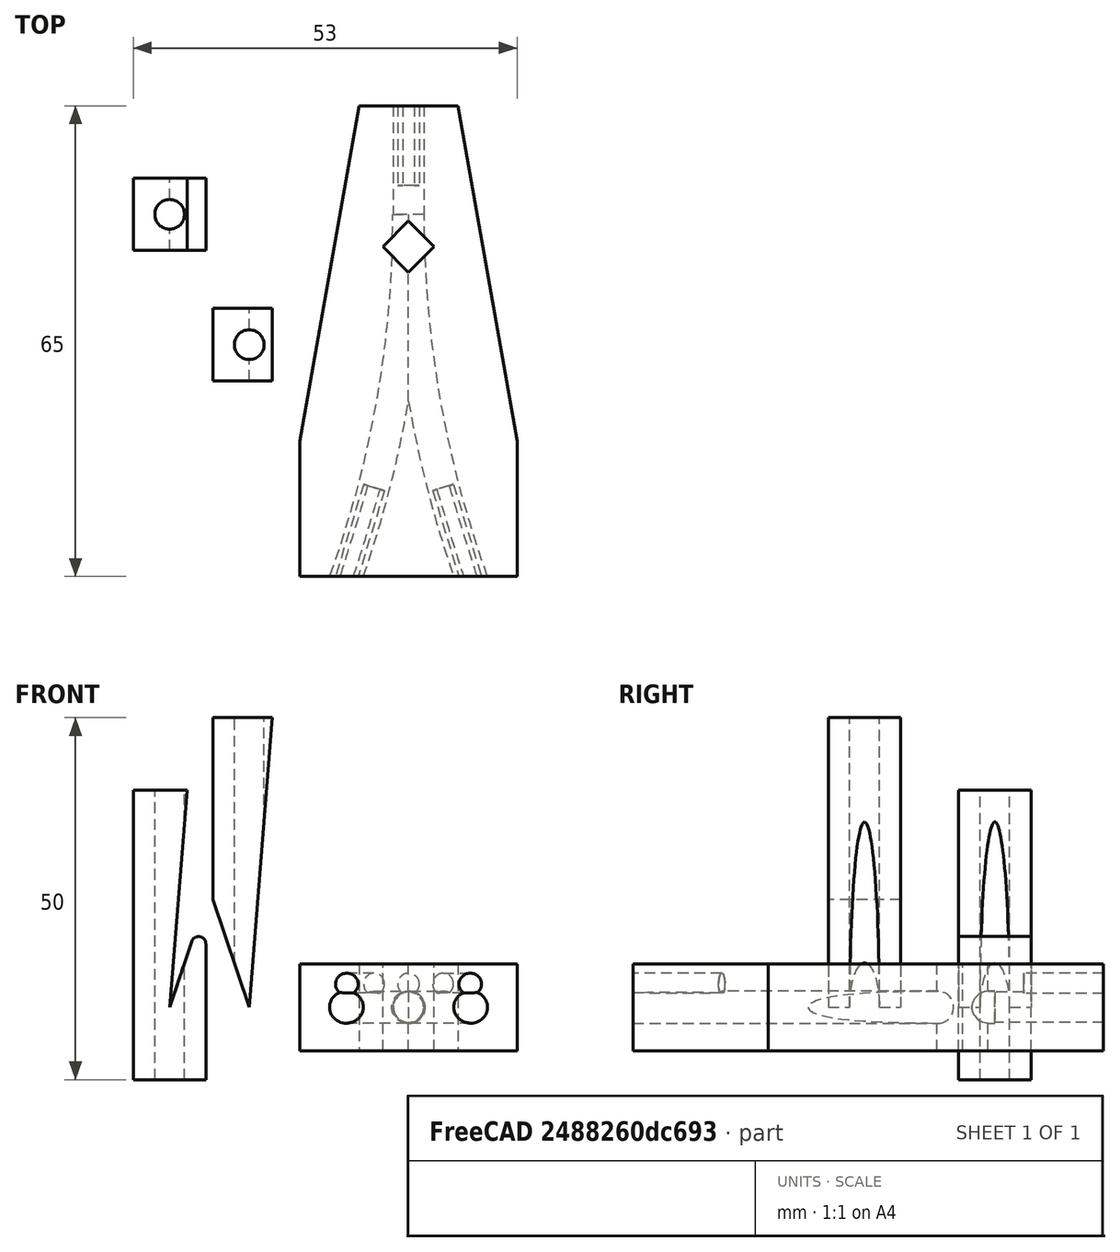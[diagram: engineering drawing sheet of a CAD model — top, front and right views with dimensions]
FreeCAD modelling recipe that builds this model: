
FCSTD DOCUMENT  (FreeCAD 0.15R4671 (Git))
Label: ptfe-traintracks
License: All rights reserved
LicenseURL: http://en.wikipedia.org/wiki/All_rights_reserved
objects: Part::Cut×17, Part::Box×12, Part::Cylinder×6, Part::Torus×2, Part::Fillet×1, Part::Mirroring×1
note: 39 computed .brp shape members not serialized (recipe doc carries the construction recipe); baked Part::Feature solids carry a one-line shape summary decoded from their .brp

FEATURE [Part::Torus] Torus
  Angle1 = -180
  Angle2 = 180
  Angle3 = 360
  Placement = pos=(-150,0,0) rot=(0,0,1;0rad)
  Radius1 = 150
  Radius2 = 2.2
FEATURE [Part::Torus] Torus001
  Angle1 = -180
  Angle2 = 180
  Angle3 = 360
  Placement = pos=(150,0,0) rot=(0,0,1;0rad)
  Radius1 = 150
  Radius2 = 2.2
FEATURE [Part::Box] Box  label="Cube"
  Height = 10
  Length = 700
  Placement = pos=(-350,0,-4) rot=(0,0,1;0rad)
  Width = 300
FEATURE [Part::Box] Box001  label="Cube001"
  Height = 10
  Length = 700
  Placement = pos=(-350,0,-4) rot=(0,0,1;0rad)
  Width = 300
FEATURE [Part::Cut] Cut
  Base = -> Torus001
  Tool = -> Box001
FEATURE [Part::Cut] Cut001
  Base = -> Torus
  Tool = -> Box
FEATURE [Part::Cylinder] Cylinder
  Angle = 360
  Height = 20
  Placement = pos=(0,20,0) rot=(1,0,0;1.5708rad)
  Radius = 2.1
FEATURE [Part::Box] Box002  label="Cube002"
  Height = 12
  Length = 30
  Placement = pos=(-15,-50,-6) rot=(0,0,1;0rad)
  Width = 65
FEATURE [Part::Cylinder] Cylinder001  label="grub"
  Angle = 360
  Height = 16
  Placement = pos=(4.76732,-37.7222,3.2) rot=(0.978386,0.146221,0.146221;1.59265rad)
  Radius = 1.5
FEATURE [Part::Cut] Cut002
  Base = -> Box002
  Tool = -> Cut
FEATURE [Part::Cut] Cut003
  Base = -> Cut002
  Tool = -> Cut001
FEATURE [Part::Cut] Cut004
  Base = -> Cut003
  Tool = -> Cylinder
FEATURE [Part::Cylinder] Cylinder005  label="grub001"
  Angle = 360
  Height = 17
  Placement = pos=(-4.76732,-37.7222,3.2) rot=(0.978386,-0.146221,-0.146221;1.59265rad)
  Radius = 1.5
FEATURE [Part::Cylinder] Cylinder006  label="grub002"
  Angle = 360
  Height = 13
  Placement = pos=(0,17,3.2) rot=(1,0,0;1.5708rad)
  Radius = 1.5
FEATURE [Part::Cut] Cut005
  Base = -> Cut004
  Tool = -> Cylinder005
FEATURE [Part::Cut] Cut006
  Base = -> Cut005
  Tool = -> Cylinder001
FEATURE [Part::Cut] Cut007
  Base = -> Cut006
  Tool = -> Cylinder006
FEATURE [Part::Box] Box003  label="Cube003"
  Height = 17
  Length = 5
  Placement = pos=(0,-8,-9) rot=(0,0,1;0.785398rad)
  Width = 5
FEATURE [Part::Cut] Cut008
  Base = -> Cut007
  Tool = -> Box003
FEATURE [Part::Box] Box004  label="Cube004"
  Height = 18
  Length = 24
  Placement = pos=(16,-37,-9) rot=(0,0,1;0.174533rad)
  Width = 60
FEATURE [Part::Box] Box005  label="Cube005"
  Height = 18
  Length = 24
  Placement = pos=(-39.6354,-32.8324,-9) rot=(0,0,-1;0.174533rad)
  Width = 60
FEATURE [Part::Cut] Cut009
  Base = -> Cut008
  Tool = -> Box004
FEATURE [Part::Cut] Cut010  label="y-block"
  Base = -> Cut009
  Tool = -> Box005
FEATURE [Part::Cylinder] Cylinder007  label="Cylinder001"
  Angle = 360
  Height = 100
  Placement = pos=(0,0,-27) rot=(0,0,1;0rad)
  Radius = 2.05
FEATURE [Part::Box] Box006  label="Cube006"
  Height = 40
  Length = 10
  Placement = pos=(-5,-5,-10) rot=(0,0,1;0rad)
  Width = 10
FEATURE [Part::Box] Box007  label="Cube007"
  Height = 33
  Length = 10
  Placement = pos=(0,-11,0) rot=(0,1,0;0.324177rad)
  Width = 22
FEATURE [Part::Box] Box008  label="Cube008"
  Height = 33
  Length = 10
  Placement = pos=(0,-11,0) rot=(0,1,0;0.079831rad)
  Width = 22
FEATURE [Part::Cut] Cut011
  Base = -> Box008
  Tool = -> Box007
FEATURE [Part::Cut] Cut012
  Base = -> Box006
  Tool = -> Cut011
FEATURE [Part::Fillet] Fillet
  Base = -> Cut012
  Edges = 1 edges r=1: [Edge17]
FEATURE [Part::Cut] Cut013  label="tube-cut-1"
  Base = -> Fillet
  Placement = pos=(-33,0,0) rot=(0,0,1;0rad)
  Tool = -> Cylinder007
FEATURE [Part::Box] Box009  label="Cube009"
  Height = 33
  Length = 10
  Placement = pos=(0,-11,0) rot=(0,1,0;0.324177rad)
  Width = 22
FEATURE [Part::Box] Box010  label="Cube010"
  Height = 45
  Length = 10
  Placement = pos=(0,-11,0) rot=(0,1,0;0.079831rad)
  Width = 22
FEATURE [Part::Cylinder] Cylinder008  label="Cylinder002"
  Angle = 360
  Height = 100
  Placement = pos=(0,0,-27) rot=(0,0,1;0rad)
  Radius = 2.05
FEATURE [Part::Mirroring] Part__Mirroring  label="Cube009 (Mirror #1)"
  Base = (0,0,0)
  Normal = (1,0,0)
  Source = -> Box009
FEATURE [Part::Box] Box011  label="Cube011"
  Height = 40
  Length = 10
  Placement = pos=(-5,-5,0) rot=(0,0,1;0rad)
  Width = 10
FEATURE [Part::Cut] Cut014
  Base = -> Box011
  Tool = -> Box010
FEATURE [Part::Cut] Cut015
  Base = -> Cut014
  Tool = -> Part__Mirroring
FEATURE [Part::Cut] Cut016  label="tube-cut-2"
  Base = -> Cut015
  Placement = pos=(-22,-18,0) rot=(0,0,1;0rad)
  Tool = -> Cylinder008
